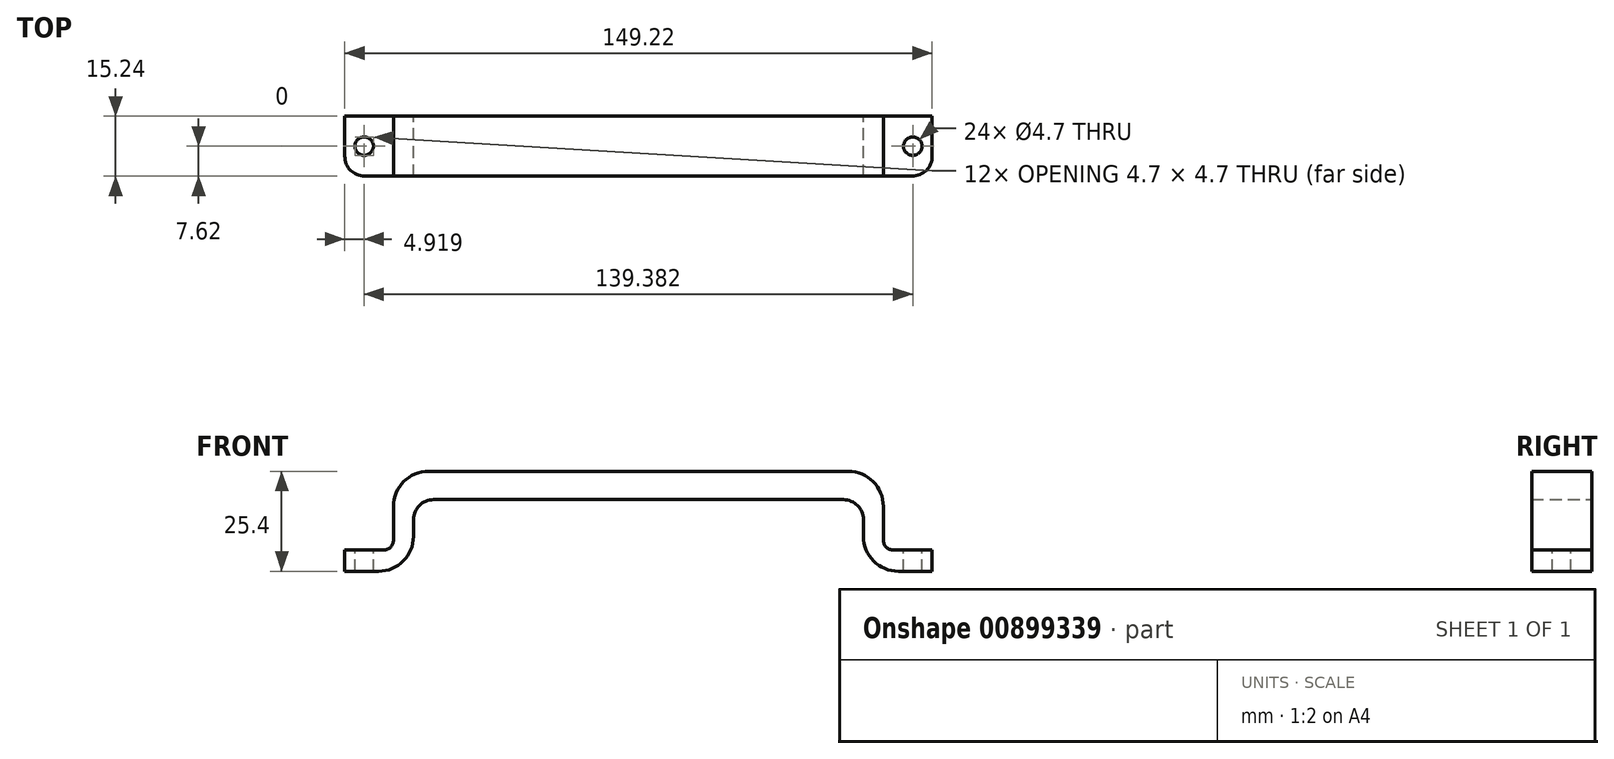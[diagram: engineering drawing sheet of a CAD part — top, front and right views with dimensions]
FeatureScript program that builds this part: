
annotation { "Feature Type Name" : "Feature", "Feature Type Description" : "" }
export const myFeature = defineFeature(function(context is Context, id is Id, definition is map)
    precondition{}
    {
        {
            var Q0;
            Q0=qCreatedBy(makeId("Front.planeOp"),FACE);
            var sketch = newSketch(context, id + "F0", { "sketchPlane" : qUnion([Q0])});
            skLineSegment(sketch, "E0", {"start": v(-53.34, 25.4) * mm, "end": v(53.34, 25.4) * mm});
            skLineSegment(sketch, "E1", {"start": v(62.23, 16.51) * mm, "end": v(62.23, 7.92) * mm});
            skLineSegment(sketch, "E2", {"start": v(64.77, 5.38) * mm, "end": v(74.61, 5.38) * mm});
            skLineSegment(sketch, "E3", {"start": v(74.61, 5.38) * mm, "end": v(74.61, 0) * mm});
            skLineSegment(sketch, "E4", {"start": v(74.61, 0) * mm, "end": v(66.04, 0) * mm});
            skLineSegment(sketch, "E5", {"start": v(57.15, 8.89) * mm, "end": v(57.15, 13.13) * mm});
            skLineSegment(sketch, "E6", {"start": v(52.07, 18.21) * mm, "end": v(-52.07, 18.21) * mm});
            skLineSegment(sketch, "E7", {"start": v(-57.15, 13.13) * mm, "end": v(-57.15, 8.9) * mm});
            skLineSegment(sketch, "E8", {"start": v(-66.04, 0) * mm, "end": v(-74.61, 0) * mm});
            skLineSegment(sketch, "E9", {"start": v(-74.61, 0) * mm, "end": v(-74.61, 5.38) * mm});
            skLineSegment(sketch, "E10", {"start": v(-74.61, 5.38) * mm, "end": v(-64.77, 5.38) * mm});
            skLineSegment(sketch, "E11", {"start": v(-62.23, 7.92) * mm, "end": v(-62.23, 16.51) * mm});
            skPoint(sketch, "E12.visualSharp", {"position": v(-57.15, 0) * mm});
            skArc(sketch, "E12.filletArc", {"start": v(-66.04, 0) * mm, "mid": v(-59.75, 2.6) * mm, "end": v(-57.15, 8.9) * mm});
            skPoint(sketch, "E13.visualSharp", {"position": v(57.15, 0) * mm});
            skArc(sketch, "E13.filletArc", {"start": v(57.15, 8.89) * mm, "mid": v(59.75, 2.6) * mm, "end": v(66.04, 0) * mm});
            skPoint(sketch, "E14.visualSharp", {"position": v(62.23, 5.38) * mm});
            skArc(sketch, "E14.filletArc", {"start": v(62.23, 7.92) * mm, "mid": v(62.97, 6.13) * mm, "end": v(64.77, 5.38) * mm});
            skPoint(sketch, "E15.visualSharp", {"position": v(-62.23, 5.38) * mm});
            skArc(sketch, "E15.filletArc", {"start": v(-64.77, 5.38) * mm, "mid": v(-62.97, 6.13) * mm, "end": v(-62.23, 7.92) * mm});
            skPoint(sketch, "E16.visualSharp", {"position": v(-57.15, 18.21) * mm});
            skArc(sketch, "E16.filletArc", {"start": v(-52.07, 18.21) * mm, "mid": v(-55.66, 16.72) * mm, "end": v(-57.15, 13.13) * mm});
            skPoint(sketch, "E17.visualSharp", {"position": v(57.15, 18.21) * mm});
            skArc(sketch, "E17.filletArc", {"start": v(57.15, 13.13) * mm, "mid": v(55.66, 16.72) * mm, "end": v(52.07, 18.21) * mm});
            skPoint(sketch, "E18.visualSharp", {"position": v(62.23, 25.4) * mm});
            skArc(sketch, "E18.filletArc", {"start": v(62.23, 16.51) * mm, "mid": v(59.63, 22.8) * mm, "end": v(53.34, 25.4) * mm});
            skPoint(sketch, "E19.visualSharp", {"position": v(-62.23, 25.4) * mm});
            skArc(sketch, "E19.filletArc", {"start": v(-53.34, 25.4) * mm, "mid": v(-59.63, 22.8) * mm, "end": v(-62.23, 16.51) * mm});
            skSolve(sketch);
        }
        {
            var Q0;
            Q0=makeQuery(id+"F0.imprint","IMPRINT",FACE,{"disambiguationData":[TD([[makeQuery(id+"F0.imprint","IMPRINT",EDGE,{"derivedFrom":sQuery(id+"F0.wireOp",EDGE,"E0")}),-1.0]])]});
            extrude(context, id + "F1", {"entities" : qUnion([Q0]), "depth" : 15.24 * mm, "offsetDistance" : 25.4 * mm});
        }
        {
            var Q0;
            Q0=makeQuery(id+"F1.opExtrude","CAP_EDGE",EDGE,{"disambiguationData":[OSD([sQuery(id+"F0.wireOp",EDGE,"E9")])],"isStart":false});
            var Q1;
            Q1=makeQuery(id+"F1.opExtrude","CAP_EDGE",EDGE,{"disambiguationData":[OSD([sQuery(id+"F0.wireOp",EDGE,"E3")])],"isStart":false});
            fillet(context, id + "F2", {"entities" : qUnion([Q0, Q1]), "radius" : 5.08 * mm, "tangentPropagation" : true, "allowEdgeOverflow" : false});
        }
        {
            var Q0;
            Q0=makeQuery(id+"F1.opExtrude","SWEPT_FACE",FACE,{"disambiguationData":[OSD([sQuery(id+"F0.wireOp",EDGE,"E10")])]});
            var sketch = newSketch(context, id + "F3", { "sketchPlane" : qUnion([Q0])});
            skCircle(sketch, "E20", {"center": v(-69.7, -7.62) * mm, "radius": 2.35 * mm});
            skPoint(sketch, "E20.centerSnap0", {"position": v(-69.7, 0) * mm});
            skPoint(sketch, "E20.centerSnap1", {"position": v(-64.77, -7.62) * mm});
            skSolve(sketch);
        }
        {
            var Q0;
            Q0=makeQuery(id+"F1.opExtrude","SWEPT_FACE",FACE,{"disambiguationData":[OSD([sQuery(id+"F0.wireOp",EDGE,"E2")])]});
            var sketch = newSketch(context, id + "F4", { "sketchPlane" : qUnion([Q0])});
            skCircle(sketch, "E21", {"center": v(69.7, -7.62) * mm, "radius": 2.35 * mm});
            skPoint(sketch, "E21.centerSnap0", {"position": v(64.77, -7.62) * mm});
            skPoint(sketch, "E21.centerSnap1", {"position": v(69.7, 0) * mm});
            skSolve(sketch);
        }
        {
            var Q0;
            Q0=sQuery(id+"F3.wireOp",VERTEX,"E20.center");
            var Q1;
            Q1=sQuery(id+"F4.wireOp",VERTEX,"E21.center");
            var Q2;
            Q2=makeQuery(id+"F1.opExtrude","SWEPT_BODY",BODY,{"disambiguationData":[OSD([sQuery(id+"F0.wireOp",EDGE,"E0"),sQuery(id+"F0.wireOp",EDGE,"E1"),sQuery(id+"F0.wireOp",EDGE,"E2"),sQuery(id+"F0.wireOp",EDGE,"E3"),sQuery(id+"F0.wireOp",EDGE,"E4"),sQuery(id+"F0.wireOp",EDGE,"E5"),sQuery(id+"F0.wireOp",EDGE,"E6"),sQuery(id+"F0.wireOp",EDGE,"E7"),sQuery(id+"F0.wireOp",EDGE,"E8"),sQuery(id+"F0.wireOp",EDGE,"E9"),sQuery(id+"F0.wireOp",EDGE,"E10"),sQuery(id+"F0.wireOp",EDGE,"E11"),sQuery(id+"F0.wireOp",EDGE,"E12.filletArc"),sQuery(id+"F0.wireOp",EDGE,"E13.filletArc"),sQuery(id+"F0.wireOp",EDGE,"E14.filletArc"),sQuery(id+"F0.wireOp",EDGE,"E15.filletArc"),sQuery(id+"F0.wireOp",EDGE,"E16.filletArc"),sQuery(id+"F0.wireOp",EDGE,"E17.filletArc"),sQuery(id+"F0.wireOp",EDGE,"E18.filletArc"),sQuery(id+"F0.wireOp",EDGE,"E19.filletArc")])]});
            hole(context, id + "F5", {"style" : HoleStyle.SIMPLE, "endStyle" : HoleEndStyle.THROUGH, "holeDiameter" : 4.7 * mm, "majorDiameter" : 6.35 * mm, "isTappedThrough" : true, "tappedDepth" : 12.7 * mm, "tapClearance" : 3, "locations" : qUnion([Q0, Q1]), "scope" : qUnion([Q2])});
        }
    });
